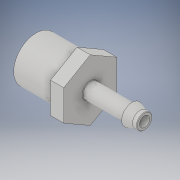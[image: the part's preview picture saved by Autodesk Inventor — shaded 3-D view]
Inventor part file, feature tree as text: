
AUTODESK INVENTOR PART (.ipt)
format: ipt  version: 2019.4 (Build 234330000, 330)  size: 1,986,560 bytes
history: native  units: mm
features: fillet x1
ambient origin geometry x8: Origin, YZ Plane, XZ Plane, XY Plane, X Axis, Y Axis, Z Axis, Center Point
bodies: Solid1 (feature_tree)
feature tree (1):
  fillet  "Fillet2"  [1 undecoded]
note: 1 required parameter value undecoded (feature->parameter linkage not recoverable at this tier; creation-order binding heuristic only, values carry confidence <= 0.55)
